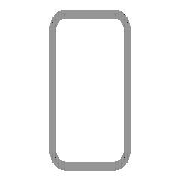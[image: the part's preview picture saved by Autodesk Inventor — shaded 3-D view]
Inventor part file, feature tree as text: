
AUTODESK INVENTOR PART (.ipt)
format: ipt  version: 2025.3 (Build 293356030, 356C)  size: 150,016 bytes
history: native  units: mm (DEFAULTED — no unit token found)
features: other x4, plane x3, split x2, sketch x1
ambient origin geometry x8: Origin, YZ Plane, XZ Plane, XY Plane, X Axis, Y Axis, Z Axis, Center Point
bodies: Solid1 (feature_tree), Body (feature_tree)
feature tree (10):
  parser-record x1  (decoder bookkeeping rows leaked as tree rows — omitted from the tree; the rows remain in map.json)
  other  "Driven Length"
  other  "Start Plane"
  other  "End Plane"
  plane  "Work Plane4"
  split  "Split1"
  plane  "Work Plane5"
  split  "Split2"
  sketch  "Sketch3"  dims[d3=2701.920698mm d4=0.0mm d7=4.0mm d9=20.0mm d11=40.0mm d12=2.0mm d13=77.445959mm d14=2779.366657mm d15=10.0mm d16=20.0mm d17=90.0deg d18=2701.920698mm]
  plane  "Work Plane3"
